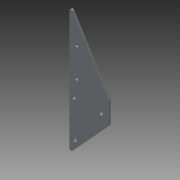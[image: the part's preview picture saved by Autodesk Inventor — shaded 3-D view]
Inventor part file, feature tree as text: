
AUTODESK INVENTOR PART (.ipt)
format: ipt  version: 2013 (Build 170138000, 138)  size: 121,856 bytes
history: native  units: in
note: dims shown in document units (in); Inventor stores cm internally (conversion verified against a paired STEP export)
features: extrude x5, sketch x5, fillet x3
ambient origin geometry x8: Origin, YZ Plane, XZ Plane, XY Plane, X Axis, Y Axis, Z Axis, Center Point
bodies: Solid1 (feature_tree)
feature tree (13):
  extrude  "Extrusion1"  Depth=6.0in
  extrude  "Extrusion2"  Depth=0.28in
  fillet  "Fillet1"  Radius=0.28in
  extrude  "Extrusion3"  Depth=0.5in
  fillet  "Fillet2"  Radius=0.56in
  fillet  "Fillet3"  Radius=0.31in
  extrude  "Extrusion4"  Depth=0.125in
  extrude  "Extrusion5"  Depth=0.266in
  sketch  "Sketch1"  dims[d1=1.5in d2=6.0in]
  sketch  "Sketch2"  dims[d3=0.125in d4=0.0in d5=0.28in d6=0.28in]
  sketch  "Sketch3"  dims[d7=0.5in d8=0.5in d9=0.56in d11=0.31in]
  sketch  "Sketch4"  dims[d12=1.0in d13=0.0in d14=0.125in]
  sketch  "Sketch5"  dims[d15=0.266in d16=0.266in d17=0.5in d18=0.5in d19=1.737in d20=2.0in d21=1.0in d22=0.0in d23=0.125in d24=3.0in d25=2.75in d26=2.75in d27=0.125in d28=0.266in d29=3.75in d30=0.375in d31=1.0in d32=0.0in d33=1.0in d34=0.0in]
